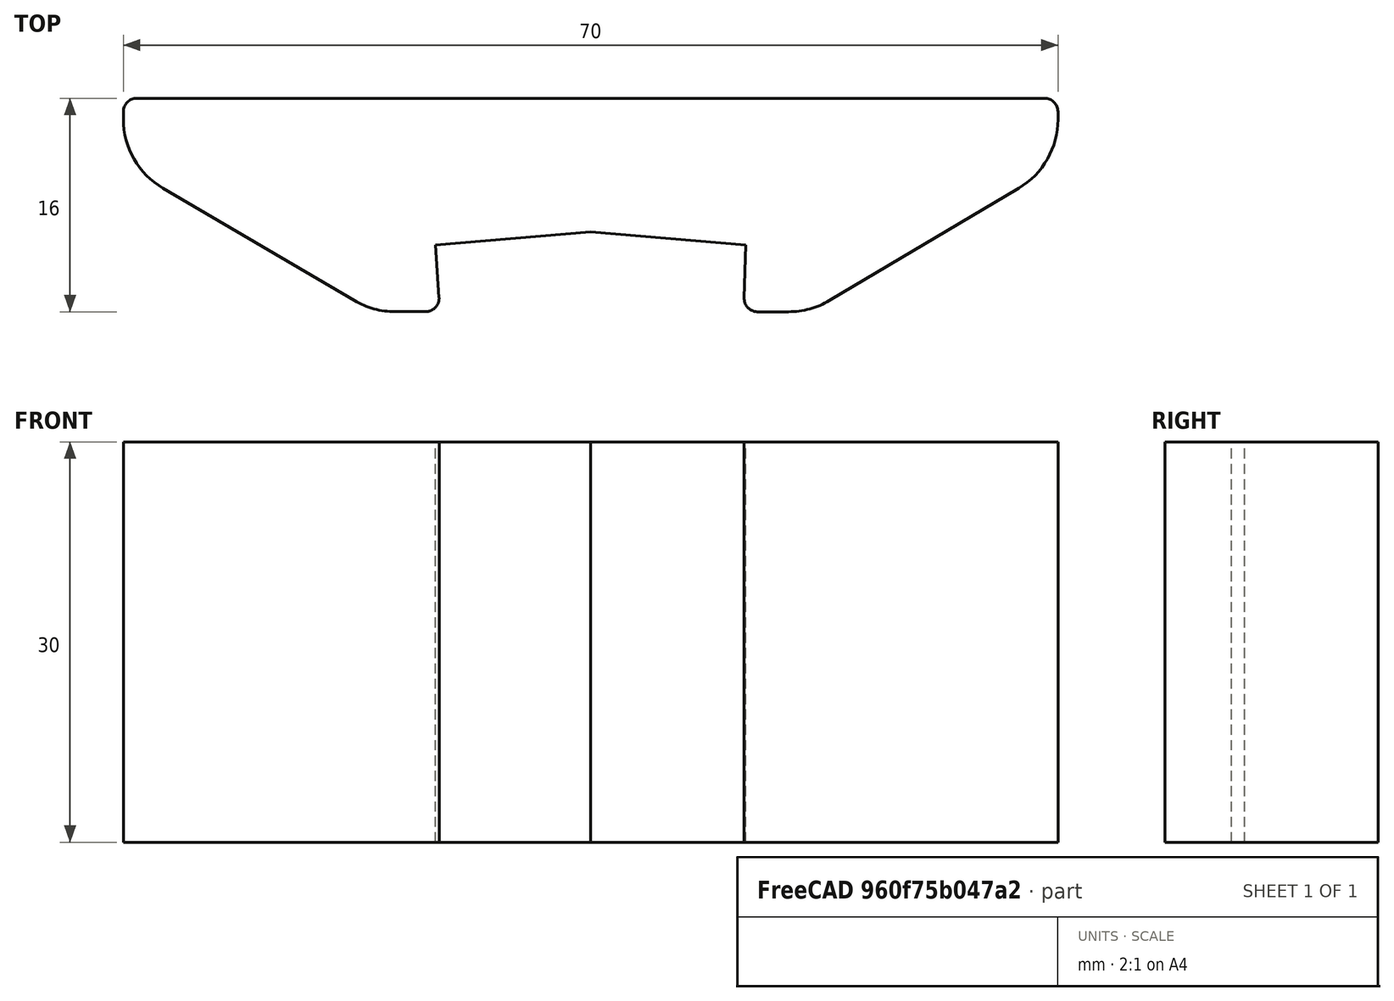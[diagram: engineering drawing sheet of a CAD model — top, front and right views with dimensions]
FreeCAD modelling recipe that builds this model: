
FCSTD DOCUMENT  (FreeCAD 0.19R)
Label: peeler
License: All rights reserved
LicenseURL: http://en.wikipedia.org/wiki/All_rights_reserved
objects: PartDesign::Fillet×2, Sketcher::SketchObject×1, PartDesign::Pad×1, PartDesign::Body×1, Mesh::Feature×1
note: 8 computed .brp shape members not serialized (recipe doc carries the construction recipe); baked Part::Feature solids carry a one-line shape summary decoded from their .brp

FEATURE [Sketcher::SketchObject] Sketch
  FullyConstrained = false
  MapMode = 5
  Support = -> [XY_Plane]
  sketch-geometry (11):
    g0: LineSegment StartX=11.625 StartY=-11 StartZ=0 EndX=11.4649 EndY=-15.9974 EndZ=0
    g1: LineSegment StartX=11.4649 StartY=-15.9974 StartZ=0 EndX=16.4649 EndY=-15.9974 EndZ=0
    g2: LineSegment StartX=16.4649 StartY=-15.9974 StartZ=0 EndX=35 EndY=-5 EndZ=0
    g3: LineSegment StartX=35 StartY=-5 StartZ=0 EndX=35 EndY=0 EndZ=0
    g4: LineSegment StartX=35 StartY=0 StartZ=0 EndX=-35 EndY=0 EndZ=0
    g5: LineSegment StartX=-35 StartY=0 StartZ=0 EndX=-35 EndY=-5 EndZ=0
    g6: LineSegment StartX=-35 StartY=-5 StartZ=0 EndX=-16.2851 EndY=-15.9884 EndZ=0
    g7: LineSegment StartX=-16.2851 StartY=-15.9884 StartZ=0 EndX=-11.2851 EndY=-15.9884 EndZ=0
    g8: LineSegment StartX=-11.2851 StartY=-15.9884 StartZ=0 EndX=-11.625 EndY=-11 EndZ=0
    g9: LineSegment StartX=-11.625 StartY=-11 StartZ=0 EndX=0 EndY=-10 EndZ=0
    g10: LineSegment StartX=0 StartY=-10 StartZ=0 EndX=11.625 EndY=-11 EndZ=0
  constraints (30):
    c: Coincident(g0,g1)
    c: Coincident(g1,g2)
    c: Coincident(g2,g3)
    c: Coincident(g3,g4)
    c: PointOnObject(g4,g-1)
    c: Coincident(g4,g5)
    c: Coincident(g5,g6)
    c: Coincident(g6,g7)
    c: Coincident(g7,g8)
    c: Vertical(g5)
    c: Vertical(g3)
    c: Horizontal(g1)
    c: Horizontal(g7)
    c: Equal(g5,g3)
    c: Equal(g8,g0)
    c: Equal(g1,g7)
    c: Symmetric(g0,g8,g-2)
    c: Symmetric(g3,g4,g-2)
    c: Distance(g4) = 70
    c: Distance(g0) = 5
    c: Distance(g7) = 5
    c: DistanceY(g0) = -11
    c: Distance(g5) = 5
    c: Coincident(g8,g9)
    c: PointOnObject(g9,g-2)
    c: Coincident(g9,g10)
    c: Coincident(g10,g0)
    c: DistanceY(g9) = -10
    c: Distance(g0,g8) = 23.25
    c: Distance(g7,g0) = 22.75
FEATURE [PartDesign::Pad] Pad
  Direction = (1,1,1)
  Length = 30
  Length2 = 100
  Profile = -> Sketch
  Type = 0
FEATURE [PartDesign::Fillet] Fillet
  Base = -> Pad [Edge17,Edge20,Edge5,Edge8]
  BaseFeature = -> Pad
  Radius = 6
  SupportTransform = false
FEATURE [PartDesign::Fillet] Fillet001
  Base = -> Fillet [Edge3,Edge40,Edge41,Edge39]
  BaseFeature = -> Fillet
  Radius = 1
  SupportTransform = false
FEATURE [PartDesign::Body] Body
  Group = -> [Sketch,Pad,Fillet,Fillet001]
  Origin = -> Origin
  Tip = -> Fillet001
FEATURE [Mesh::Feature] Mesh  label="Fillet001 (Meshed)"
